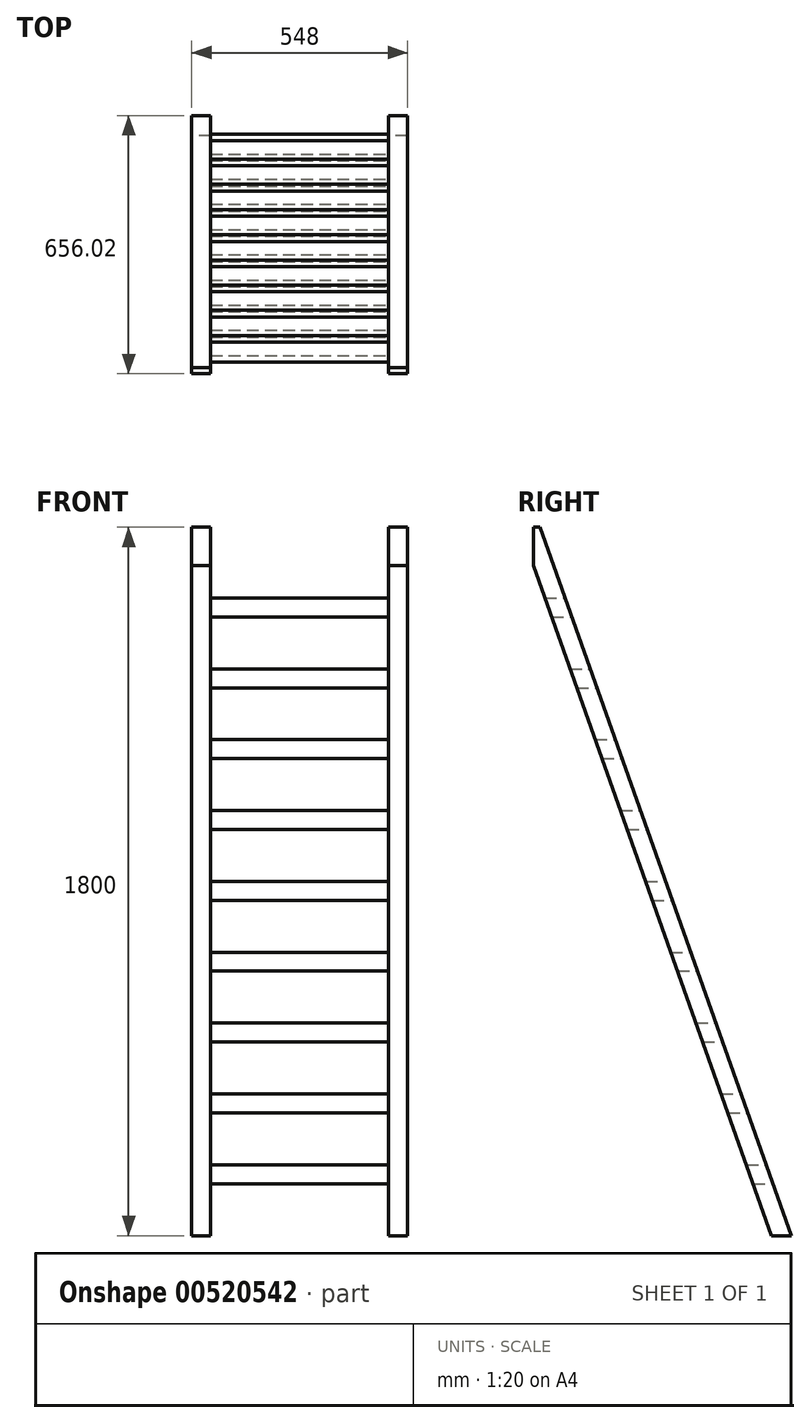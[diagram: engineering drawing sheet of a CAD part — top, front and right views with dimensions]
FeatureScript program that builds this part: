
annotation { "Feature Type Name" : "Feature", "Feature Type Description" : "" }
export const myFeature = defineFeature(function(context is Context, id is Id, definition is map)
    precondition{}
    {
        {
            var Q0;
            Q0=qCreatedBy(makeId("Right.planeOp"),FACE);
            var sketch = newSketch(context, id + "F0", { "sketchPlane" : qUnion([Q0])});
            skLineSegment(sketch, "E0.bottom", {"start": v(649.06, 0) * mm, "end": v(700, 0) * mm});
            skLineSegment(sketch, "E1", {"start": v(700, 0) * mm, "end": v(60.09, 1800) * mm});
            skLineSegment(sketch, "E2", {"start": v(60.09, 1800) * mm, "end": v(43.98, 1800) * mm});
            skLineSegment(sketch, "E3.0", {"start": v(649.06, 0) * mm, "end": v(43.98, 1702) * mm});
            skLineSegment(sketch, "E4", {"start": v(43.98, 1702) * mm, "end": v(43.98, 1800) * mm});
            skLineSegment(sketch, "E5.0", {"start": v(585.07, 180) * mm, "end": v(636, 180) * mm});
            skLineSegment(sketch, "E6.0", {"start": v(602.13, 132) * mm, "end": v(653.07, 132) * mm});
            skLineSegment(sketch, "E7.0", {"start": v(521.07, 360) * mm, "end": v(572.02, 360) * mm});
            skLineSegment(sketch, "E8.0", {"start": v(538.14, 312) * mm, "end": v(589.08, 312) * mm});
            skLineSegment(sketch, "E9.0", {"start": v(457.08, 540) * mm, "end": v(508.03, 540) * mm});
            skLineSegment(sketch, "E10.0", {"start": v(474.15, 492) * mm, "end": v(525.1, 492) * mm});
            skLineSegment(sketch, "E11.0", {"start": v(393.1, 720) * mm, "end": v(444.03, 720) * mm});
            skLineSegment(sketch, "E12.0", {"start": v(410.16, 672) * mm, "end": v(461.1, 672) * mm});
            skLineSegment(sketch, "E13.0", {"start": v(329.1, 900) * mm, "end": v(380.04, 900) * mm});
            skLineSegment(sketch, "E14.0", {"start": v(346.16, 852) * mm, "end": v(397.1, 852) * mm});
            skLineSegment(sketch, "E15.0", {"start": v(265.1, 1080) * mm, "end": v(316.05, 1080) * mm});
            skLineSegment(sketch, "E16.0", {"start": v(282.17, 1032) * mm, "end": v(333.12, 1032) * mm});
            skLineSegment(sketch, "E17.0", {"start": v(201.12, 1260) * mm, "end": v(252.06, 1260) * mm});
            skLineSegment(sketch, "E18.0", {"start": v(218.18, 1212) * mm, "end": v(269.12, 1212) * mm});
            skLineSegment(sketch, "E19.0", {"start": v(137.13, 1440) * mm, "end": v(188.07, 1440) * mm});
            skLineSegment(sketch, "E20.0", {"start": v(154.2, 1392) * mm, "end": v(205.13, 1392) * mm});
            skLineSegment(sketch, "E21.0", {"start": v(73.13, 1620) * mm, "end": v(124.08, 1620) * mm});
            skLineSegment(sketch, "E22.0", {"start": v(90.2, 1572) * mm, "end": v(141.14, 1572) * mm});
            skSolve(sketch);
        }
        {
            var Q0;
            {var subQ0=sQuery(id+"F0.wireOp",EDGE,"E5.0");Q0=makeQuery(id+"F0.imprint","IMPRINT",FACE,{"disambiguationData":[TD([[makeQuery(id+"F0.imprint","IMPRINT",EDGE,{"derivedFrom":subQ0}),1.0]])]});}
            var Q1;
            {var subQ0=sQuery(id+"F0.wireOp",EDGE,"E9.0");Q1=makeQuery(id+"F0.imprint","IMPRINT",FACE,{"disambiguationData":[TD([[makeQuery(id+"F0.imprint","IMPRINT",EDGE,{"derivedFrom":subQ0}),-1.0]])]});}
            var Q2;
            {var subQ0=sQuery(id+"F0.wireOp",EDGE,"E15.0");Q2=makeQuery(id+"F0.imprint","IMPRINT",FACE,{"disambiguationData":[TD([[makeQuery(id+"F0.imprint","IMPRINT",EDGE,{"derivedFrom":subQ0}),-1.0]])]});}
            var Q3;
            {var subQ0=sQuery(id+"F0.wireOp",EDGE,"E19.0");Q3=makeQuery(id+"F0.imprint","IMPRINT",FACE,{"disambiguationData":[TD([[makeQuery(id+"F0.imprint","IMPRINT",EDGE,{"derivedFrom":subQ0}),1.0]])]});}
            var Q4;
            {var subQ0=sQuery(id+"F0.wireOp",EDGE,"E11.0");Q4=makeQuery(id+"F0.imprint","IMPRINT",FACE,{"disambiguationData":[TD([[makeQuery(id+"F0.imprint","IMPRINT",EDGE,{"derivedFrom":subQ0}),1.0]])]});}
            var Q5;
            {var subQ0=sQuery(id+"F0.wireOp",EDGE,"E21.0");Q5=makeQuery(id+"F0.imprint","IMPRINT",FACE,{"disambiguationData":[TD([[makeQuery(id+"F0.imprint","IMPRINT",EDGE,{"derivedFrom":subQ0}),-1.0]])]});}
            var Q6;
            {var subQ0=sQuery(id+"F0.wireOp",EDGE,"E7.0");Q6=makeQuery(id+"F0.imprint","IMPRINT",FACE,{"disambiguationData":[TD([[makeQuery(id+"F0.imprint","IMPRINT",EDGE,{"derivedFrom":subQ0}),1.0]])]});}
            var Q7;
            {var subQ0=sQuery(id+"F0.wireOp",EDGE,"E9.0");Q7=makeQuery(id+"F0.imprint","IMPRINT",FACE,{"disambiguationData":[TD([[makeQuery(id+"F0.imprint","IMPRINT",EDGE,{"derivedFrom":subQ0}),1.0]])]});}
            var Q8;
            {var subQ0=sQuery(id+"F0.wireOp",EDGE,"E13.0");Q8=makeQuery(id+"F0.imprint","IMPRINT",FACE,{"disambiguationData":[TD([[makeQuery(id+"F0.imprint","IMPRINT",EDGE,{"derivedFrom":subQ0}),1.0]])]});}
            var Q9;
            {var subQ1=sQuery(id+"F0.wireOp",EDGE,"E2");Q9=makeQuery(id+"F0.imprint","IMPRINT",FACE,{"disambiguationData":[TD([[makeQuery(id+"F0.imprint","IMPRINT",EDGE,{"derivedFrom":subQ1}),1.0]])]});}
            var Q10;
            {var subQ0=sQuery(id+"F0.wireOp",EDGE,"E5.0");Q10=makeQuery(id+"F0.imprint","IMPRINT",FACE,{"disambiguationData":[TD([[makeQuery(id+"F0.imprint","IMPRINT",EDGE,{"derivedFrom":subQ0}),-1.0]])]});}
            var Q11;
            {var subQ0=sQuery(id+"F0.wireOp",EDGE,"E11.0");Q11=makeQuery(id+"F0.imprint","IMPRINT",FACE,{"disambiguationData":[TD([[makeQuery(id+"F0.imprint","IMPRINT",EDGE,{"derivedFrom":subQ0}),-1.0]])]});}
            var Q12;
            {var subQ0=sQuery(id+"F0.wireOp",EDGE,"E0.bottom");Q12=makeQuery(id+"F0.imprint","IMPRINT",FACE,{"disambiguationData":[TD([[makeQuery(id+"F0.imprint","IMPRINT",EDGE,{"derivedFrom":subQ0}),1.0]])]});}
            var Q13;
            {var subQ0=sQuery(id+"F0.wireOp",EDGE,"E17.0");Q13=makeQuery(id+"F0.imprint","IMPRINT",FACE,{"disambiguationData":[TD([[makeQuery(id+"F0.imprint","IMPRINT",EDGE,{"derivedFrom":subQ0}),-1.0]])]});}
            var Q14;
            {var subQ0=sQuery(id+"F0.wireOp",EDGE,"E15.0");Q14=makeQuery(id+"F0.imprint","IMPRINT",FACE,{"disambiguationData":[TD([[makeQuery(id+"F0.imprint","IMPRINT",EDGE,{"derivedFrom":subQ0}),1.0]])]});}
            var Q15;
            {var subQ0=sQuery(id+"F0.wireOp",EDGE,"E17.0");Q15=makeQuery(id+"F0.imprint","IMPRINT",FACE,{"disambiguationData":[TD([[makeQuery(id+"F0.imprint","IMPRINT",EDGE,{"derivedFrom":subQ0}),1.0]])]});}
            var Q16;
            {var subQ0=sQuery(id+"F0.wireOp",EDGE,"E13.0");Q16=makeQuery(id+"F0.imprint","IMPRINT",FACE,{"disambiguationData":[TD([[makeQuery(id+"F0.imprint","IMPRINT",EDGE,{"derivedFrom":subQ0}),-1.0]])]});}
            var Q17;
            {var subQ0=sQuery(id+"F0.wireOp",EDGE,"E7.0");Q17=makeQuery(id+"F0.imprint","IMPRINT",FACE,{"disambiguationData":[TD([[makeQuery(id+"F0.imprint","IMPRINT",EDGE,{"derivedFrom":subQ0}),-1.0]])]});}
            var Q18;
            {var subQ0=sQuery(id+"F0.wireOp",EDGE,"E19.0");Q18=makeQuery(id+"F0.imprint","IMPRINT",FACE,{"disambiguationData":[TD([[makeQuery(id+"F0.imprint","IMPRINT",EDGE,{"derivedFrom":subQ0}),-1.0]])]});}
            extrude(context, id + "F1", {"entities" : qUnion([Q0, Q1, Q2, Q3, Q4, Q5, Q6, Q7, Q8, Q9, Q10, Q11, Q12, Q13, Q14, Q15, Q16, Q17, Q18]), "oppositeDirection" : true, "depth" : -48 * mm, "offsetDistance" : 25 * mm});
        }
        {
            var Q0;
            Q0=makeQuery(id+"F1.opExtrude","SWEPT_BODY",BODY,{"disambiguationData":[OSD([sQuery(id+"F0.wireOp",EDGE,"E0.bottom"),sQuery(id+"F0.wireOp",EDGE,"E1"),sQuery(id+"F0.wireOp",EDGE,"E2"),sQuery(id+"F0.wireOp",EDGE,"E3.0"),sQuery(id+"F0.wireOp",EDGE,"E4")])]});
            transform(context, id + "F2", {"entities" : qUnion([Q0]), "transformType" : TransformType.TRANSLATION_3D, "dx" : -500 * mm, "dy" : 0 * mm, "dz" : 0 * mm, "makeCopy" : true});
        }
        {
            var Q0;
            {var subQ0=sQuery(id+"F0.wireOp",EDGE,"E5.0");Q0=makeQuery(id+"F0.imprint","IMPRINT",FACE,{"disambiguationData":[TD([[makeQuery(id+"F0.imprint","IMPRINT",EDGE,{"derivedFrom":subQ0}),-1.0]])]});}
            var Q1;
            {var subQ0=sQuery(id+"F0.wireOp",EDGE,"E7.0");Q1=makeQuery(id+"F0.imprint","IMPRINT",FACE,{"disambiguationData":[TD([[makeQuery(id+"F0.imprint","IMPRINT",EDGE,{"derivedFrom":subQ0}),-1.0]])]});}
            var Q2;
            {var subQ0=sQuery(id+"F0.wireOp",EDGE,"E9.0");Q2=makeQuery(id+"F0.imprint","IMPRINT",FACE,{"disambiguationData":[TD([[makeQuery(id+"F0.imprint","IMPRINT",EDGE,{"derivedFrom":subQ0}),-1.0]])]});}
            var Q3;
            {var subQ0=sQuery(id+"F0.wireOp",EDGE,"E11.0");Q3=makeQuery(id+"F0.imprint","IMPRINT",FACE,{"disambiguationData":[TD([[makeQuery(id+"F0.imprint","IMPRINT",EDGE,{"derivedFrom":subQ0}),-1.0]])]});}
            var Q4;
            {var subQ0=sQuery(id+"F0.wireOp",EDGE,"E13.0");Q4=makeQuery(id+"F0.imprint","IMPRINT",FACE,{"disambiguationData":[TD([[makeQuery(id+"F0.imprint","IMPRINT",EDGE,{"derivedFrom":subQ0}),-1.0]])]});}
            var Q5;
            {var subQ0=sQuery(id+"F0.wireOp",EDGE,"E15.0");Q5=makeQuery(id+"F0.imprint","IMPRINT",FACE,{"disambiguationData":[TD([[makeQuery(id+"F0.imprint","IMPRINT",EDGE,{"derivedFrom":subQ0}),-1.0]])]});}
            var Q6;
            {var subQ0=sQuery(id+"F0.wireOp",EDGE,"E17.0");Q6=makeQuery(id+"F0.imprint","IMPRINT",FACE,{"disambiguationData":[TD([[makeQuery(id+"F0.imprint","IMPRINT",EDGE,{"derivedFrom":subQ0}),-1.0]])]});}
            var Q7;
            {var subQ0=sQuery(id+"F0.wireOp",EDGE,"E19.0");Q7=makeQuery(id+"F0.imprint","IMPRINT",FACE,{"disambiguationData":[TD([[makeQuery(id+"F0.imprint","IMPRINT",EDGE,{"derivedFrom":subQ0}),-1.0]])]});}
            var Q8;
            {var subQ0=sQuery(id+"F0.wireOp",EDGE,"E21.0");Q8=makeQuery(id+"F0.imprint","IMPRINT",FACE,{"disambiguationData":[TD([[makeQuery(id+"F0.imprint","IMPRINT",EDGE,{"derivedFrom":subQ0}),-1.0]])]});}
            extrude(context, id + "F3", {"entities" : qUnion([Q0, Q1, Q2, Q3, Q4, Q5, Q6, Q7, Q8]), "depth" : -452 * mm, "offsetDistance" : 25 * mm});
        }
    });
